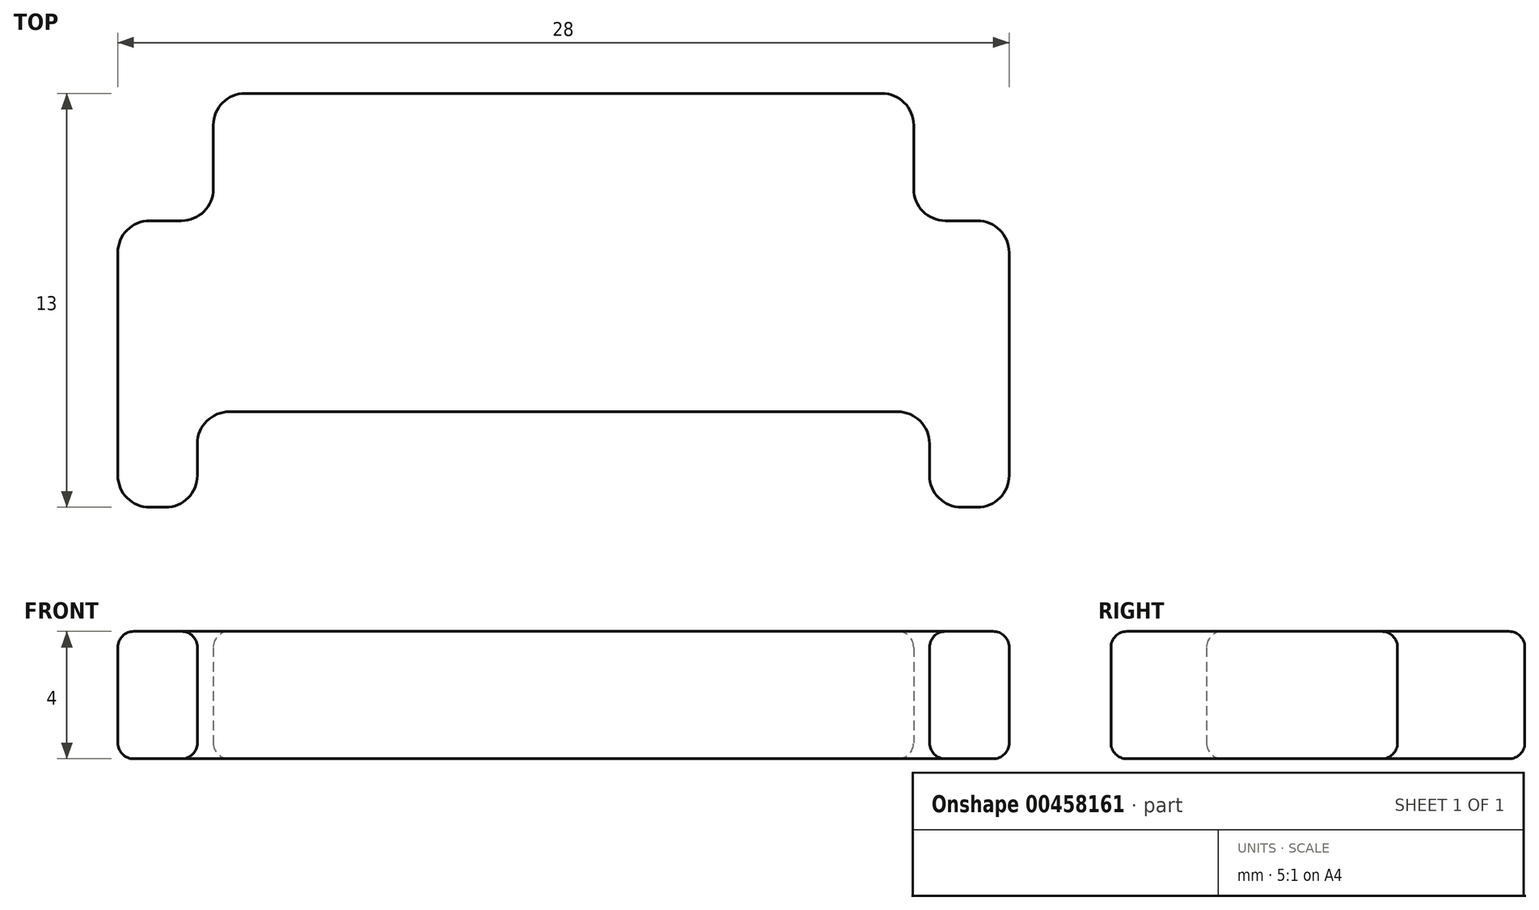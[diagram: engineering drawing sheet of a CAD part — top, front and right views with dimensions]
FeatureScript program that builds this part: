
annotation { "Feature Type Name" : "Feature", "Feature Type Description" : "" }
export const myFeature = defineFeature(function(context is Context, id is Id, definition is map)
    precondition{}
    {
        {
            var Q0;
            Q0=qCreatedBy(makeId("Top.planeOp"),FACE);
            var sketch = newSketch(context, id + "F0", { "sketchPlane" : qUnion([Q0])});
            skLineSegment(sketch, "E0", {"start": v(11, -4) * mm, "end": v(14, -4) * mm});
            skLineSegment(sketch, "E1", {"start": v(14, -4) * mm, "end": v(14, -13) * mm});
            skLineSegment(sketch, "E2", {"start": v(14, -13) * mm, "end": v(11.5, -13) * mm});
            skLineSegment(sketch, "E3", {"start": v(11.5, -13) * mm, "end": v(11.5, -10) * mm});
            skLineSegment(sketch, "E4", {"start": v(11.5, -10) * mm, "end": v(-11.5, -10) * mm});
            skLineSegment(sketch, "E5", {"start": v(-11.5, -13) * mm, "end": v(-14, -13) * mm});
            skLineSegment(sketch, "E6", {"start": v(-14, -13) * mm, "end": v(-14, -4) * mm});
            skLineSegment(sketch, "E7", {"start": v(-14, -4) * mm, "end": v(-11, -4) * mm});
            skLineSegment(sketch, "E8", {"start": v(-11, -4) * mm, "end": v(-11, 0) * mm});
            skLineSegment(sketch, "E9", {"start": v(11, 0) * mm, "end": v(11, -4) * mm});
            skLineSegment(sketch, "E10", {"start": v(-11, 0) * mm, "end": v(11, 0) * mm});
            skLineSegment(sketch, "E11", {"start": v(-11.5, -10) * mm, "end": v(-11.5, -13) * mm});
            skSolve(sketch);
        }
        {
            var Q0;
            Q0=makeQuery(id+"F0.imprint","IMPRINT",FACE,{"disambiguationData":[TD([[makeQuery(id+"F0.imprint","IMPRINT",EDGE,{"derivedFrom":sQuery(id+"F0.wireOp",EDGE,"E0")}),-1.0]])]});
            extrude(context, id + "F1", {"entities" : qUnion([Q0]), "depth" : 4 * mm});
        }
        {
            var Q0;
            Q0=makeQuery(id+"F1.opExtrude","SWEPT_EDGE",EDGE,{"disambiguationData":[OSD([sQuery(id+"F0.wireOp",EDGE,"E5"),sQuery(id+"F0.wireOp",EDGE,"E11")])]});
            var Q1;
            Q1=makeQuery(id+"F1.opExtrude","SWEPT_EDGE",EDGE,{"disambiguationData":[OSD([sQuery(id+"F0.wireOp",EDGE,"E2"),sQuery(id+"F0.wireOp",EDGE,"E3")])]});
            var Q2;
            Q2=makeQuery(id+"F1.opExtrude","SWEPT_EDGE",EDGE,{"disambiguationData":[OSD([sQuery(id+"F0.wireOp",EDGE,"E5"),sQuery(id+"F0.wireOp",EDGE,"E6")])]});
            var Q3;
            Q3=makeQuery(id+"F1.opExtrude","SWEPT_EDGE",EDGE,{"disambiguationData":[OSD([sQuery(id+"F0.wireOp",EDGE,"E4"),sQuery(id+"F0.wireOp",EDGE,"E11")])]});
            var Q4;
            Q4=makeQuery(id+"F1.opExtrude","SWEPT_EDGE",EDGE,{"disambiguationData":[OSD([sQuery(id+"F0.wireOp",EDGE,"E1"),sQuery(id+"F0.wireOp",EDGE,"E2")])]});
            var Q5;
            Q5=makeQuery(id+"F1.opExtrude","SWEPT_EDGE",EDGE,{"disambiguationData":[OSD([sQuery(id+"F0.wireOp",EDGE,"E3"),sQuery(id+"F0.wireOp",EDGE,"E4")])]});
            var Q6;
            Q6=makeQuery(id+"F1.opExtrude","SWEPT_EDGE",EDGE,{"disambiguationData":[OSD([sQuery(id+"F0.wireOp",EDGE,"E0"),sQuery(id+"F0.wireOp",EDGE,"E1")])]});
            var Q7;
            Q7=makeQuery(id+"F1.opExtrude","SWEPT_EDGE",EDGE,{"disambiguationData":[OSD([sQuery(id+"F0.wireOp",EDGE,"E0"),sQuery(id+"F0.wireOp",EDGE,"E9")])]});
            var Q8;
            Q8=makeQuery(id+"F1.opExtrude","SWEPT_EDGE",EDGE,{"disambiguationData":[OSD([sQuery(id+"F0.wireOp",EDGE,"E9"),sQuery(id+"F0.wireOp",EDGE,"E10")])]});
            var Q9;
            Q9=makeQuery(id+"F1.opExtrude","SWEPT_EDGE",EDGE,{"disambiguationData":[OSD([sQuery(id+"F0.wireOp",EDGE,"E8"),sQuery(id+"F0.wireOp",EDGE,"E10")])]});
            var Q10;
            Q10=makeQuery(id+"F1.opExtrude","SWEPT_EDGE",EDGE,{"disambiguationData":[OSD([sQuery(id+"F0.wireOp",EDGE,"E7"),sQuery(id+"F0.wireOp",EDGE,"E8")])]});
            var Q11;
            Q11=makeQuery(id+"F1.opExtrude","SWEPT_EDGE",EDGE,{"disambiguationData":[OSD([sQuery(id+"F0.wireOp",EDGE,"E6"),sQuery(id+"F0.wireOp",EDGE,"E7")])]});
            fillet(context, id + "F2", {"entities" : qUnion([Q0, Q1, Q2, Q3, Q4, Q5, Q6, Q7, Q8, Q9, Q10, Q11]), "radius" : 1 * mm, "tangentPropagation" : true, "allowEdgeOverflow" : false});
        }
        {
            var Q0;
            Q0=makeQuery(id+"F1.opExtrude","CAP_EDGE",EDGE,{"disambiguationData":[OSD([sQuery(id+"F0.wireOp",EDGE,"E6")])],"isStart":false});
            var Q1;
            Q1=makeQuery(id+"F1.opExtrude","CAP_EDGE",EDGE,{"disambiguationData":[OSD([sQuery(id+"F0.wireOp",EDGE,"E6")])],"isStart":true});
            fillet(context, id + "F3", {"entities" : qUnion([Q0, Q1]), "radius" : 0.5 * mm, "tangentPropagation" : true, "allowEdgeOverflow" : false});
        }
    });
